# Revit family: MAG-MEGARACK-611_1
name_source: partatom
category: Furniture
revit_build: Autodesk Revit 2014 (Build: 20130308_1515(x64)
units: mm (PartAtom-declared; Revit-internal decimal feet)

## types (2) — shared parameters
# Of Racks = 4
# of Hangers = 5
Assembly Code = E2020200
Cap Finish = MAG - Plastic Black
Caster Finish = MAG - Plastic Black
Depth = 25"
Frame Finish = MAG - Powdercoat White
Hanger Finish = MAG - Powdercoat White
Hangers Dist = 6 1/2"
Height = 61 3/4"
Keynote = 12500
Low Emitting Finish = Yes
Low Emitting Material = Yes
Manufacturer = Magnuson Group
Rack Array Dist = 3 11/64"
Salvage or Reuse = Yes
Type Comments = Megarack
URL = https://magnusongroup.com
Width = 72"
zero-valued in all types: Percentage of Recycled Content

## per-type parameters (varying)
| type | Hangers | Racks |
| MR-611H | No | Yes |
| MR-611K | Yes | No |

note: column(s) folded — value = type name in every type: Description, Model

## geometry (parser evidence)
native form markers: Sweep x9
no freeform markers — native parametric forms only
